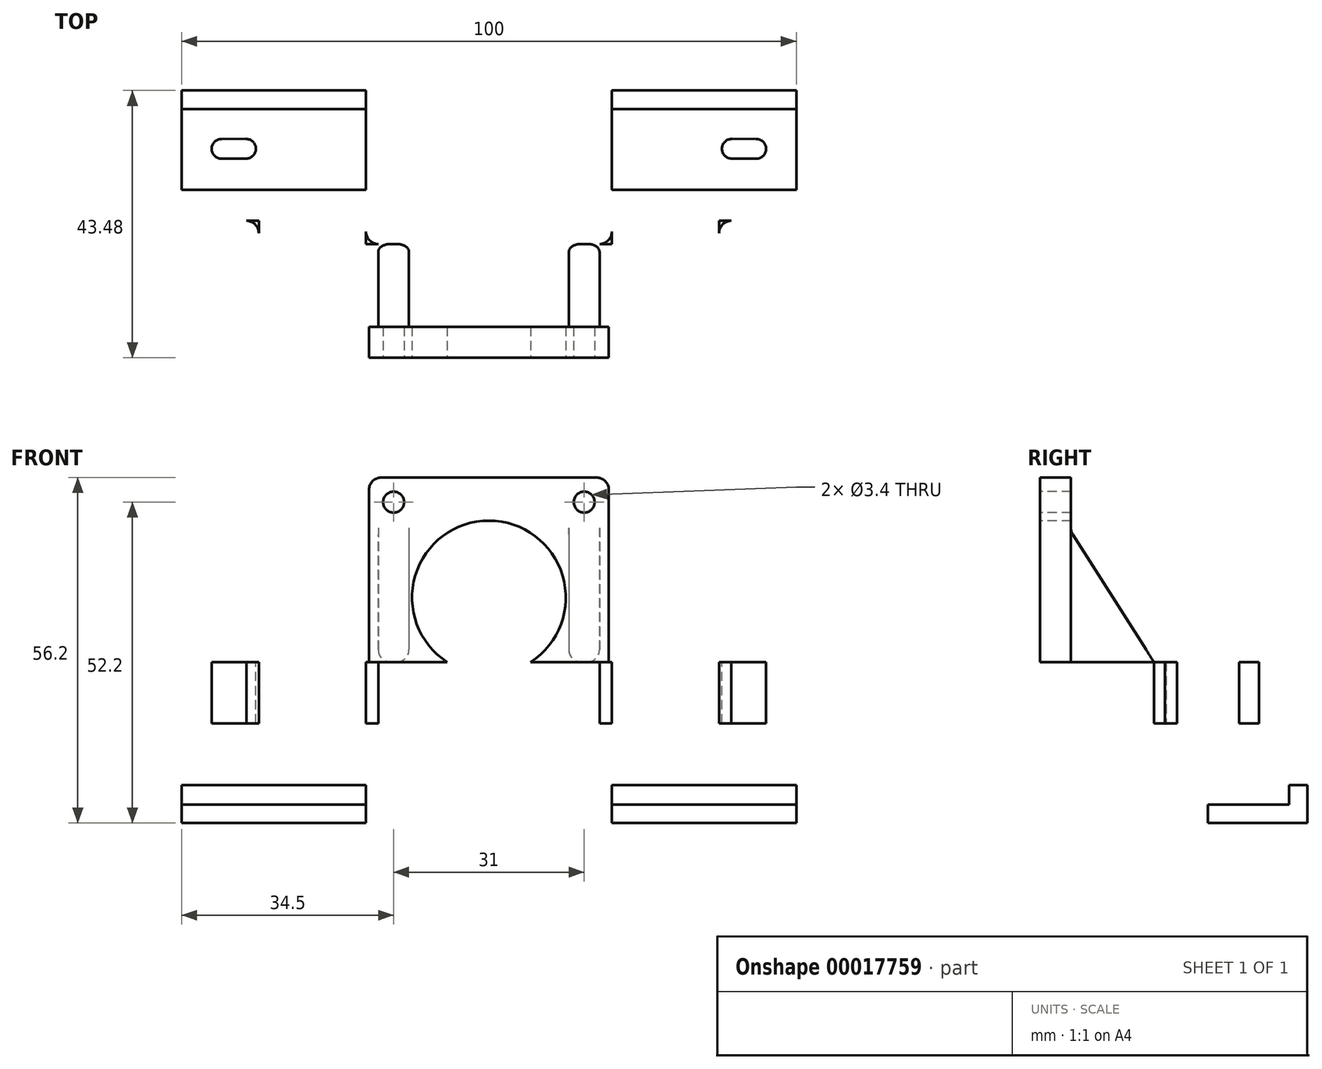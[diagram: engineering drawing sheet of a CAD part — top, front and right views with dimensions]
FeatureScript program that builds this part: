
annotation { "Feature Type Name" : "Feature", "Feature Type Description" : "" }
export const myFeature = defineFeature(function(context is Context, id is Id, definition is map)
    precondition{}
    {
        {
            var Q0;
            Q0=qCreatedBy(makeId("Top.planeOp"),FACE);
            var sketch = newSketch(context, id + "F0", { "sketchPlane" : qUnion([Q0])});
            skLineSegment(sketch, "E0", {"start": v(0, -13.82) * mm, "end": v(-37.44, -13.82) * mm});
            skLineSegment(sketch, "E1", {"start": v(-37.44, -13.82) * mm, "end": v(-37.44, 8.46) * mm});
            skLineSegment(sketch, "E2", {"start": v(-37.44, 8.46) * mm, "end": v(-50, 8.46) * mm});
            skLineSegment(sketch, "E3", {"start": v(-50, 8.46) * mm, "end": v(-50, 13.46) * mm});
            skLineSegment(sketch, "E4", {"start": v(-50, 13.46) * mm, "end": v(-20, 13.46) * mm});
            skLineSegment(sketch, "E5", {"start": v(-20, 13.46) * mm, "end": v(-20, 4.68) * mm});
            skLineSegment(sketch, "E6", {"start": v(-20, 4.68) * mm, "end": v(0, 4.68) * mm});
            skLineSegment(sketch, "E7", {"start": v(0, 4.68) * mm, "end": v(0, -13.82) * mm});
            skLineSegment(sketch, "E8.0", {"start": v(-18.87, 13.46) * mm, "end": v(-18.87, 4.68) * mm, "construction": true});
            skSolve(sketch);
        }
        {
            var Q0;
            Q0=qSketchRegion(id+"F0",true);
            extrude(context, id + "F1", {"entities" : qUnion([Q0]), "depth" : 10 * mm});
        }
        {
            var Q0;
            Q0=makeQuery(id+"F1.opExtrude","SWEPT_FACE",FACE,{"disambiguationData":[OSD([sQuery(id+"F0.wireOp",EDGE,"E0")])]});
            var sketch = newSketch(context, id + "F2", { "sketchPlane" : qUnion([Q0])});
            skLineSegment(sketch, "E9", {"start": v(0, 5) * mm, "end": v(0, 5) * mm});
            skCircle(sketch, "E10", {"center": v(-15.5, 5) * mm, "radius": 1.6 * mm});
            skSolve(sketch);
        }
        {
            var Q0;
            Q0=qSketchRegion(id+"F2",true);
            extrude(context, id + "F3", {"entities" : qUnion([Q0]), "operationType" : NewBodyOperationType.REMOVE, "endBound" : BoundingType.THROUGH_ALL, "oppositeDirection" : true, "depth" : 25 * mm});
        }
        {
            var Q0;
            {var subQ0=makeQuery(id+"F1.opExtrude","CAP_FACE",FACE,{"disambiguationData":[OSD([sQuery(id+"F0.wireOp",EDGE,"E0"),sQuery(id+"F0.wireOp",EDGE,"fd64a43a-5635-4f94-a977-4dd36923accb"),sQuery(id+"F0.wireOp",EDGE,"1334f7d4-4c90-4769-8fa3-fe5f576fb005"),sQuery(id+"F0.wireOp",EDGE,"E1"),sQuery(id+"F0.wireOp",EDGE,"E2"),sQuery(id+"F0.wireOp",EDGE,"E3"),sQuery(id+"F0.wireOp",EDGE,"E4"),sQuery(id+"F0.wireOp",EDGE,"E5"),sQuery(id+"F0.wireOp",EDGE,"E6"),sQuery(id+"F0.wireOp",EDGE,"E7")])],"isStart":false});Q0=makeQuery(id+"F22.boolean.opBoolean","MERGE",FACE,{"derivedFrom":[subQ0,makeQuery(id+"F22.opPattern","COPY",FACE,{"derivedFrom":subQ0,"instanceName":"1"})]});}
            var sketch = newSketch(context, id + "F4", { "sketchPlane" : qUnion([Q0])});
            skCircle(sketch, "E11", {"center": v(-30, 1.46) * mm, "radius": 4.1 * mm});
            skLineSegment(sketch, "E12", {"start": v(-30, 1.46) * mm, "end": v(-30, -13.82) * mm, "construction": true});
            skLineSegment(sketch, "E13.bottom", {"start": v(-30.49, -2.04) * mm, "end": v(-29.51, -2.04) * mm});
            skLineSegment(sketch, "E13.top", {"start": v(-30.49, -14.16) * mm, "end": v(-29.51, -14.16) * mm});
            skLineSegment(sketch, "E13.left", {"start": v(-30.49, -2.04) * mm, "end": v(-30.49, -14.16) * mm});
            skLineSegment(sketch, "E13.right", {"start": v(-29.51, -2.04) * mm, "end": v(-29.51, -14.16) * mm});
            skPoint(sketch, "E14", {"position": v(-30, -2.04) * mm});
            skSolve(sketch);
        }
        {
            var Q0;
            Q0=qSketchRegion(id+"F4",true);
            var Q1;
            {var subQ3=sQuery(id+"F4.wireOp",EDGE,"E13.bottom");Q1=makeQuery(id+"F4.imprint","IMPRINT",FACE,{"disambiguationData":[TD([[makeQuery(id+"F4.imprint","IMPRINT",EDGE,{"derivedFrom":subQ3}),-1.0]])]});}
            extrude(context, id + "F5", {"entities" : qUnion([Q0, Q1]), "operationType" : NewBodyOperationType.REMOVE, "endBound" : BoundingType.THROUGH_ALL, "oppositeDirection" : true, "depth" : 25 * mm});
        }
        {
            var Q0;
            Q0=makeQuery(id+"F1.opExtrude","SWEPT_FACE",FACE,{"disambiguationData":[OSD([sQuery(id+"F0.wireOp",EDGE,"E1")])]});
            var sketch = newSketch(context, id + "F6", { "sketchPlane" : qUnion([Q0])});
            skCircle(sketch, "E15", {"center": v(10.1, 4.98) * mm, "radius": 1.4 * mm});
            skCircle(sketch, "E16", {"center": v(10.1, 4.98) * mm, "radius": 1.7 * mm});
            skSolve(sketch);
        }
        {
            var Q0;
            Q0=makeQuery(id+"F6.imprint","IMPRINT",FACE,{"disambiguationData":[TD([[makeQuery(id+"F6.imprint","IMPRINT",EDGE,{"derivedFrom":sQuery(id+"F6.wireOp",EDGE,"E15")}),1.0]])]});
            extrude(context, id + "F7", {"entities" : qUnion([Q0]), "operationType" : NewBodyOperationType.REMOVE, "oppositeDirection" : true, "depth" : 18 * mm});
        }
        {
            var Q0;
            Q0=makeQuery(id+"F1.opExtrude","CAP_FACE",FACE,{"disambiguationData":[OSD([sQuery(id+"F0.wireOp",EDGE,"E0"),sQuery(id+"F0.wireOp",EDGE,"E1"),sQuery(id+"F0.wireOp",EDGE,"E2"),sQuery(id+"F0.wireOp",EDGE,"E3"),sQuery(id+"F0.wireOp",EDGE,"E4"),sQuery(id+"F0.wireOp",EDGE,"E5"),sQuery(id+"F0.wireOp",EDGE,"E6"),sQuery(id+"F0.wireOp",EDGE,"E7")])],"isStart":false});
            var sketch = newSketch(context, id + "F8", { "sketchPlane" : qUnion([Q0])});
            skLineSegment(sketch, "E17.0", {"start": v(-19.51, -2.61) * mm, "end": v(-19.51, -13.82) * mm, "construction": true});
            skLineSegment(sketch, "E18.bottom", {"start": v(-19.51, -13.82) * mm, "end": v(0, -13.82) * mm});
            skLineSegment(sketch, "E18.top", {"start": v(-19.51, -8.82) * mm, "end": v(0, -8.82) * mm});
            skLineSegment(sketch, "E18.left", {"start": v(-19.51, -13.82) * mm, "end": v(-19.51, -8.82) * mm});
            skLineSegment(sketch, "E18.right", {"start": v(0, -13.82) * mm, "end": v(0, -8.82) * mm});
            skSolve(sketch);
        }
        {
            var Q0;
            Q0=makeQuery(id+"F6.imprint","IMPRINT",FACE,{"disambiguationData":[TD([[makeQuery(id+"F6.imprint","IMPRINT",EDGE,{"derivedFrom":sQuery(id+"F6.wireOp",EDGE,"E15")}),1.0]])]});
            var Q1;
            Q1=makeQuery(id+"F6.imprint","IMPRINT",FACE,{"disambiguationData":[TD([[makeQuery(id+"F6.imprint","IMPRINT",EDGE,{"derivedFrom":sQuery(id+"F6.wireOp",EDGE,"E15")}),-1.0]])]});
            extrude(context, id + "F9", {"entities" : qUnion([Q0, Q1]), "operationType" : NewBodyOperationType.REMOVE, "endBound" : BoundingType.UP_TO_NEXT, "oppositeDirection" : true, "depth" : 25 * mm});
        }
        {
            var Q0;
            Q0=makeQuery(id+"F1.opExtrude","SWEPT_FACE",FACE,{"disambiguationData":[OSD([sQuery(id+"F0.wireOp",EDGE,"E3")])]});
            var sketch = newSketch(context, id + "F10", { "sketchPlane" : qUnion([Q0])});
            skLineSegment(sketch, "E19", {"start": v(-13.46, 0) * mm, "end": v(-26.66, 0) * mm});
            skLineSegment(sketch, "E20", {"start": v(-26.66, 0) * mm, "end": v(-26.66, -13.2) * mm});
            skLineSegment(sketch, "E21", {"start": v(-29.66, -13.2) * mm, "end": v(-29.66, 10) * mm});
            skLineSegment(sketch, "E22", {"start": v(-29.66, 10) * mm, "end": v(-13.46, 10) * mm});
            skLineSegment(sketch, "E23", {"start": v(-26.66, -13.2) * mm, "end": v(-13.46, -13.2) * mm});
            skLineSegment(sketch, "E24", {"start": v(-13.46, -13.2) * mm, "end": v(-13.46, -16.2) * mm});
            skLineSegment(sketch, "E25", {"start": v(-13.46, -16.2) * mm, "end": v(-29.66, -16.2) * mm});
            skLineSegment(sketch, "E26", {"start": v(-29.66, -16.2) * mm, "end": v(-29.66, -13.2) * mm});
            skSolve(sketch);
        }
        {
            var Q0;
            Q0=makeQuery(id+"F10.imprint","IMPRINT",FACE,{"disambiguationData":[TD([[makeQuery(id+"F10.imprint","IMPRINT",EDGE,{"derivedFrom":sQuery(id+"F10.wireOp",EDGE,"E19")}),-1.0]])]});
            var Q1;
            Q1=makeQuery(id+"F1.opExtrude","SWEPT_FACE",FACE,{"disambiguationData":[OSD([sQuery(id+"F0.wireOp",EDGE,"E5")])]});
            extrude(context, id + "F11", {"entities" : qUnion([Q0]), "operationType" : NewBodyOperationType.ADD, "endBound" : BoundingType.UP_TO_SURFACE, "oppositeDirection" : true, "endBoundEntityFace" : qUnion([Q1]), "depth" : 25 * mm});
        }
        {
            var Q0;
            {var subQ0=makeQuery(id+"F1.opExtrude","CAP_FACE",FACE,{"disambiguationData":[OSD([sQuery(id+"F0.wireOp",EDGE,"E0"),sQuery(id+"F0.wireOp",EDGE,"E1"),sQuery(id+"F0.wireOp",EDGE,"E2"),sQuery(id+"F0.wireOp",EDGE,"E3"),sQuery(id+"F0.wireOp",EDGE,"E4"),sQuery(id+"F0.wireOp",EDGE,"E5"),sQuery(id+"F0.wireOp",EDGE,"E6"),sQuery(id+"F0.wireOp",EDGE,"E7")])],"isStart":false});Q0=makeQuery(id+"F11.boolean.opBoolean","MERGE",FACE,{"derivedFrom":[subQ0,makeQuery(id+"F22.opPattern","COPY",FACE,{"derivedFrom":subQ0,"instanceName":"1"}),makeQuery(id+"F11.opExtrude","SWEPT_FACE",FACE,{"disambiguationData":[OSD([sQuery(id+"F10.wireOp",EDGE,"E22")])]})]});}
            var sketch = newSketch(context, id + "F12", { "sketchPlane" : qUnion([Q0])});
            skLineSegment(sketch, "E27", {"start": v(-50, 20.16) * mm, "end": v(-43.5, 20.16) * mm, "construction": true});
            skLineSegment(sketch, "E28.0", {"start": v(-43.5, 20.16) * mm, "end": v(-39.5, 20.17) * mm});
            skArc(sketch, "E29.0.startCap", {"start": v(-43.5, 18.56) * mm, "mid": v(-45.1, 20.15) * mm, "end": v(-43.5, 21.76) * mm});
            skArc(sketch, "E29.0.endCap", {"start": v(-39.51, 21.77) * mm, "mid": v(-37.9, 20.18) * mm, "end": v(-39.5, 18.57) * mm});
            skLineSegment(sketch, "E29.0.left", {"start": v(-43.5, 21.76) * mm, "end": v(-39.51, 21.77) * mm});
            skLineSegment(sketch, "E29.0.right", {"start": v(-43.5, 18.56) * mm, "end": v(-39.5, 18.57) * mm});
            skSolve(sketch);
        }
        {
            var Q0;
            {var subQ8=sQuery(id+"F8.wireOp",EDGE,"E18.left");Q0=makeQuery(id+"F8.imprint","IMPRINT",FACE,{"disambiguationData":[TD([[makeQuery(id+"F8.imprint","IMPRINT",EDGE,{"derivedFrom":subQ8}),-1.0]])]});}
            var Q1;
            {var subQ5=sQuery(id+"F8.wireOp",EDGE,"E18.right");Q1=makeQuery(id+"F8.imprint","IMPRINT",FACE,{"disambiguationData":[TD([[makeQuery(id+"F8.imprint","IMPRINT",EDGE,{"derivedFrom":subQ5}),1.0]])]});}
            extrude(context, id + "F13", {"entities" : qUnion([Q0, Q1]), "operationType" : NewBodyOperationType.ADD, "depth" : 30 * mm});
        }
        {
            var Q0;
            {var subQ0=sQuery(id+"F0.wireOp",EDGE,"E0");var subQ1=sQuery(id+"F0.wireOp",EDGE,"E7");var subQ8=makeQuery(id+"F13.boolean.opBoolean","MERGE",FACE,{"derivedFrom":[makeQuery(id+"F5.boolean.opBoolean","SPLIT",FACE,{"disambiguationData":[TD([makeQuery(id+"F1.opExtrude","SWEPT_FACE",FACE,{"disambiguationData":[OSD([subQ1])]})])],"derivedFrom":makeQuery(id+"F1.opExtrude","SWEPT_FACE",FACE,{"disambiguationData":[OSD([subQ0])]})}),makeQuery(id+"F13.opExtrude","SWEPT_FACE",FACE,{"disambiguationData":[OSD([sQuery(id+"F8.wireOp",EDGE,"E18.bottom")])]})]});Q0=makeQuery(id+"F22.boolean.opBoolean","MERGE",FACE,{"derivedFrom":[subQ8,makeQuery(id+"F22.opPattern","COPY",FACE,{"derivedFrom":subQ8,"instanceName":"1"})]});}
            var sketch = newSketch(context, id + "F14", { "sketchPlane" : qUnion([Q0])});
            skLineSegment(sketch, "E30.0", {"start": v(29.51, 36) * mm, "end": v(-29.51, 36) * mm, "construction": true});
            skCircle(sketch, "E31", {"center": v(-15.5, 36) * mm, "radius": 1.7 * mm});
            skCircle(sketch, "E32.0", {"center": v(-15.5, 5) * mm, "radius": 1.6 * mm});
            skSolve(sketch);
        }
        {
            var Q0;
            Q0=makeQuery(id+"F14.imprint","IMPRINT",FACE,{"disambiguationData":[TD([[makeQuery(id+"F14.imprint","IMPRINT",EDGE,{"derivedFrom":sQuery(id+"F14.wireOp",EDGE,"E31")}),1.0]])]});
            extrude(context, id + "F15", {"entities" : qUnion([Q0]), "operationType" : NewBodyOperationType.REMOVE, "oppositeDirection" : true, "depth" : 25 * mm});
        }
        {
            var Q0;
            Q0=makeQuery(id+"F1.opExtrude","SWEPT_EDGE",EDGE,{"disambiguationData":[OSD([sQuery(id+"F0.wireOp",EDGE,"E0"),sQuery(id+"F0.wireOp",EDGE,"E1")])]});
            var Q1;
            Q1=makeQuery(id+"F1.opExtrude","SWEPT_EDGE",EDGE,{"disambiguationData":[OSD([sQuery(id+"F0.wireOp",EDGE,"E1"),sQuery(id+"F0.wireOp",EDGE,"E2")])]});
            var Q2;
            Q2=makeQuery(id+"F1.opExtrude","SWEPT_EDGE",EDGE,{"disambiguationData":[OSD([sQuery(id+"F0.wireOp",EDGE,"E2"),sQuery(id+"F0.wireOp",EDGE,"E3")])]});
            var Q3;
            Q3=makeQuery(id+"F13.opExtrude","CAP_EDGE",EDGE,{"disambiguationData":[OSD([sQuery(id+"F8.wireOp",EDGE,"E18.left")])],"isStart":true});
            var Q4;
            Q4=makeQuery(id+"F13.opExtrude","CAP_EDGE",EDGE,{"disambiguationData":[OSD([sQuery(id+"F8.wireOp",EDGE,"E18.left")])],"isStart":false});
            var Q5;
            Q5=makeQuery(id+"F1.opExtrude","SWEPT_EDGE",EDGE,{"disambiguationData":[OSD([sQuery(id+"F0.wireOp",EDGE,"E5"),sQuery(id+"F0.wireOp",EDGE,"E6")])]});
            fillet(context, id + "F16", {"entities" : qUnion([Q0, Q1, Q2, Q3, Q4, Q5]), "radius" : 2 * mm, "tangentPropagation" : true, "allowEdgeOverflow" : false});
        }
        {
            var Q0;
            {var subQ0=sQuery(id+"F0.wireOp",EDGE,"E0");var subQ1=sQuery(id+"F0.wireOp",EDGE,"E1");var subQ2=sQuery(id+"F0.wireOp",EDGE,"E2");var subQ3=sQuery(id+"F0.wireOp",EDGE,"E3");var subQ4=sQuery(id+"F0.wireOp",EDGE,"E4");var subQ5=sQuery(id+"F0.wireOp",EDGE,"E5");var subQ6=sQuery(id+"F0.wireOp",EDGE,"E6");var subQ7=sQuery(id+"F0.wireOp",EDGE,"E7");var subQ8=makeQuery(id+"F1.opExtrude","CAP_FACE",FACE,{"disambiguationData":[OSD([subQ0,subQ1,subQ2,subQ3,subQ4,subQ5,subQ6,subQ7])],"isStart":false});var subQ9=sQuery(id+"F10.wireOp",EDGE,"E22");var subQ10=makeQuery(id+"F11.boolean.opBoolean","MERGE",FACE,{"derivedFrom":[subQ8,makeQuery(id+"F11.opExtrude","SWEPT_FACE",FACE,{"disambiguationData":[OSD([subQ9])]})]});Q0=makeQuery(id+"F23.boolean.opBoolean","SPLIT",FACE,{"disambiguationData":[TD([makeQuery(id+"F1.opExtrude","SWEPT_FACE",FACE,{"disambiguationData":[OSD([subQ1])]})])],"derivedFrom":makeQuery(id+"F22.boolean.opBoolean","MERGE",FACE,{"derivedFrom":[subQ10,makeQuery(id+"F22.opPattern","COPY",FACE,{"derivedFrom":subQ10,"instanceName":"1"})]})});}
            var sketch = newSketch(context, id + "F17", { "sketchPlane" : qUnion([Q0])});
            skLineSegment(sketch, "E33", {"start": v(-18, 4.68) * mm, "end": v(-18, -8.82) * mm});
            skLineSegment(sketch, "E34", {"start": v(-18, 4.68) * mm, "end": v(-13, 4.68) * mm});
            skLineSegment(sketch, "E35", {"start": v(-13, 4.68) * mm, "end": v(-13, -8.82) * mm});
            skLineSegment(sketch, "E36", {"start": v(-13, -8.82) * mm, "end": v(-18, -8.82) * mm});
            skSolve(sketch);
        }
        {
            var Q0;
            Q0=makeQuery(id+"F12.imprint","IMPRINT",FACE,{"disambiguationData":[TD([[makeQuery(id+"F12.imprint","IMPRINT",EDGE,{"derivedFrom":sQuery(id+"F12.wireOp",EDGE,"E29.0.startCap")}),-1.0]])]});
            extrude(context, id + "F18", {"entities" : qUnion([Q0]), "operationType" : NewBodyOperationType.REMOVE, "oppositeDirection" : true, "depth" : 20 * mm});
        }
        {
            var Q0;
            Q0=makeQuery(id+"F17.imprint","IMPRINT",FACE,{"disambiguationData":[TD([[makeQuery(id+"F17.imprint","IMPRINT",EDGE,{"derivedFrom":sQuery(id+"F17.wireOp",EDGE,"E33")}),1.0]])]});
            extrude(context, id + "F19", {"entities" : qUnion([Q0]), "operationType" : NewBodyOperationType.ADD, "depth" : 22 * mm});
        }
        {
            var Q0;
            Q0=makeQuery(id+"F19.opExtrude","CAP_EDGE",EDGE,{"disambiguationData":[OSD([sQuery(id+"F17.wireOp",EDGE,"E34")])],"isStart":false});
            chamfer(context, id + "F20", {"entities" : qUnion([Q0]), "chamferType" : ChamferType.TWO_OFFSETS, "width1" : 22 * mm, "oppositeDirection" : false, "width2" : 14 * mm});
        }
        {
            var Q0;
            {var subQ0=sQuery(id+"F0.wireOp",EDGE,"E0");var subQ1=sQuery(id+"F0.wireOp",EDGE,"E7");var subQ8=makeQuery(id+"F13.boolean.opBoolean","MERGE",FACE,{"derivedFrom":[makeQuery(id+"F5.boolean.opBoolean","SPLIT",FACE,{"disambiguationData":[TD([makeQuery(id+"F1.opExtrude","SWEPT_FACE",FACE,{"disambiguationData":[OSD([subQ1])]})])],"derivedFrom":makeQuery(id+"F1.opExtrude","SWEPT_FACE",FACE,{"disambiguationData":[OSD([subQ0])]})}),makeQuery(id+"F13.opExtrude","SWEPT_FACE",FACE,{"disambiguationData":[OSD([sQuery(id+"F8.wireOp",EDGE,"E18.bottom")])]})]});Q0=makeQuery(id+"F22.boolean.opBoolean","MERGE",FACE,{"derivedFrom":[subQ8,makeQuery(id+"F22.opPattern","COPY",FACE,{"derivedFrom":subQ8,"instanceName":"1"})]});}
            var sketch = newSketch(context, id + "F21", { "sketchPlane" : qUnion([Q0])});
            skCircle(sketch, "E37", {"center": v(0, 20.48) * mm, "radius": 12.5 * mm});
            skLineSegment(sketch, "E38.0", {"start": v(0, 37.65) * mm, "end": v(0, 3.31) * mm, "construction": true});
            skSolve(sketch);
        }
        {
            var Q0;
            Q0=makeQuery(id+"F1.opExtrude","SWEPT_BODY",BODY,{"disambiguationData":[OSD([sQuery(id+"F0.wireOp",EDGE,"E0"),sQuery(id+"F0.wireOp",EDGE,"fd64a43a-5635-4f94-a977-4dd36923accb"),sQuery(id+"F0.wireOp",EDGE,"1334f7d4-4c90-4769-8fa3-fe5f576fb005"),sQuery(id+"F0.wireOp",EDGE,"E1"),sQuery(id+"F0.wireOp",EDGE,"E2"),sQuery(id+"F0.wireOp",EDGE,"E3"),sQuery(id+"F0.wireOp",EDGE,"E4"),sQuery(id+"F0.wireOp",EDGE,"E5"),sQuery(id+"F0.wireOp",EDGE,"E6"),sQuery(id+"F0.wireOp",EDGE,"E7")])]});
            var Q1;
            Q1=qCreatedBy(makeId("Right.planeOp"),FACE);
            mirror(context, id + "F22", {"operationType" : NewBodyOperationType.ADD, "entities" : qUnion([Q0]), "mirrorPlane" : qUnion([Q1])});
        }
        {
            var Q0;
            Q0 = qSketchRegion(id + "F21", true);
            var Q1;
            Q1=makeQuery(id+"F21.imprint","IMPRINT",FACE,{"disambiguationData":[TD([[makeQuery(id+"F21.imprint","IMPRINT",EDGE,{"derivedFrom":sQuery(id+"F21.wireOp",EDGE,"E37")}),1.0]])]});
            extrude(context, id + "F23", {"entities" : qUnion([Q0, Q1]), "operationType" : NewBodyOperationType.REMOVE, "oppositeDirection" : true, "depth" : 25 * mm});
        }
        {
            var Q0;
            Q0=makeQuery(id+"F22.opPattern","COPY",EDGE,{"derivedFrom":makeQuery(id+"F20.opChamfer","BLEND_EDGE",EDGE,{"blendedFrom":[makeQuery(id+"F19.opExtrude","CAP_EDGE",EDGE,{"disambiguationData":[OSD([sQuery(id+"F17.wireOp",EDGE,"E34")])],"isStart":false}),makeQuery(id+"F13.opExtrude","SWEPT_FACE",FACE,{"disambiguationData":[OSD([sQuery(id+"F8.wireOp",EDGE,"E18.top")])]})],"blendedInto":[makeQuery(id+"F13.opExtrude","SWEPT_FACE",FACE,{"disambiguationData":[OSD([sQuery(id+"F8.wireOp",EDGE,"E18.top")])]})]}),"instanceName":"1"});
            var Q1;
            Q1=makeQuery(id+"F20.opChamfer","BLEND_EDGE",EDGE,{"blendedFrom":[makeQuery(id+"F19.opExtrude","CAP_EDGE",EDGE,{"disambiguationData":[OSD([sQuery(id+"F17.wireOp",EDGE,"E34")])],"isStart":false}),makeQuery(id+"F13.opExtrude","SWEPT_FACE",FACE,{"disambiguationData":[OSD([sQuery(id+"F8.wireOp",EDGE,"E18.top")])]})],"blendedInto":[makeQuery(id+"F13.opExtrude","SWEPT_FACE",FACE,{"disambiguationData":[OSD([sQuery(id+"F8.wireOp",EDGE,"E18.top")])]})]});
            var Q2;
            Q2=makeQuery(id+"F19.opExtrude","CAP_EDGE",EDGE,{"disambiguationData":[OSD([sQuery(id+"F17.wireOp",EDGE,"E33")])],"isStart":true});
            var Q3;
            Q3=makeQuery(id+"F19.opExtrude","CAP_EDGE",EDGE,{"disambiguationData":[OSD([sQuery(id+"F17.wireOp",EDGE,"E35")])],"isStart":true});
            var Q4;
            Q4=makeQuery(id+"F22.opPattern","COPY",EDGE,{"derivedFrom":makeQuery(id+"F19.opExtrude","CAP_EDGE",EDGE,{"disambiguationData":[OSD([sQuery(id+"F17.wireOp",EDGE,"E35")])],"isStart":true}),"instanceName":"1"});
            var Q5;
            Q5=makeQuery(id+"F22.opPattern","COPY",EDGE,{"derivedFrom":makeQuery(id+"F19.opExtrude","CAP_EDGE",EDGE,{"disambiguationData":[OSD([sQuery(id+"F17.wireOp",EDGE,"E33")])],"isStart":true}),"instanceName":"1"});
            var Q6;
            Q6=makeQuery(id+"F22.opPattern","COPY",EDGE,{"derivedFrom":makeQuery(id+"F19.opExtrude","SWEPT_EDGE",EDGE,{"disambiguationData":[OSD([sQuery(id+"F8.wireOp",EDGE,"E18.top"),sQuery(id+"F17.wireOp",EDGE,"E33"),sQuery(id+"F17.wireOp",EDGE,"E36")])]}),"instanceName":"1"});
            var Q7;
            Q7=makeQuery(id+"F19.opExtrude","SWEPT_EDGE",EDGE,{"disambiguationData":[OSD([sQuery(id+"F8.wireOp",EDGE,"E18.top"),sQuery(id+"F17.wireOp",EDGE,"E33"),sQuery(id+"F17.wireOp",EDGE,"E36")])]});
            var Q8;
            Q8=makeQuery(id+"F22.opPattern","COPY",EDGE,{"derivedFrom":makeQuery(id+"F19.opExtrude","SWEPT_EDGE",EDGE,{"disambiguationData":[OSD([sQuery(id+"F8.wireOp",EDGE,"E18.top"),sQuery(id+"F17.wireOp",EDGE,"E35"),sQuery(id+"F17.wireOp",EDGE,"E36")])]}),"instanceName":"1"});
            var Q9;
            Q9=makeQuery(id+"F19.opExtrude","SWEPT_EDGE",EDGE,{"disambiguationData":[OSD([sQuery(id+"F8.wireOp",EDGE,"E18.top"),sQuery(id+"F17.wireOp",EDGE,"E35"),sQuery(id+"F17.wireOp",EDGE,"E36")])]});
            fillet(context, id + "F24", {"entities" : qUnion([Q0, Q1, Q2, Q3, Q4, Q5, Q6, Q7, Q8, Q9]), "radius" : 2 * mm, "tangentPropagation" : true, "allowEdgeOverflow" : false});
        }
    });
